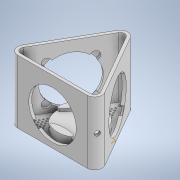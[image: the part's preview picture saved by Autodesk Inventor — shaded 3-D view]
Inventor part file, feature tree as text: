
AUTODESK INVENTOR PART (.ipt)
format: ipt  version: 2022.4 (Build 264492010, 492A)  size: 419,840 bytes
history: native  units: mm
features: sketch x11, extrude x7, pattern_circular x3, plane x2, shell x1, revolve x1, fillet x1, hole x1
ambient origin geometry x8: Origin, YZ Plane, XZ Plane, XY Plane, X Axis, Y Axis, Z Axis, Center Point
bodies: Solid1 (feature_tree)
feature tree (27):
  extrude  "Extrusion1"  Depth=37.0mm
  shell  "Shell1"  Thickness=37.0mm
  sketch  "Sketch16"  dims[d18=212.772423mm]
  extrude  "Extrusion9"  TaperAngle=30.0deg  [1 undecoded]
  sketch  "Sketch4"  dims[d12=30.0deg d13=30.0deg]
  plane  "Work Plane1"
  extrude  "Extrusion6"  TaperAngle=30.0deg  [1 undecoded]
  sketch  "Sketch11"  dims[d16=30.0deg d17=30.0deg]
  extrude  "Extrusion8"  TaperAngle=30.0deg  [1 undecoded]
  pattern_circular  "Circular Pattern3"  Angle=120.0deg  [1 undecoded]
  pattern_circular  "Circular Pattern4"  Angle=120.0deg  [1 undecoded]
  extrude  "Extrusion10"  TaperAngle=45.0deg  [1 undecoded]
  sketch  "Sketch20"  dims[d21=0.0mm]
  revolve  "Revolution4"  [1 undecoded]
  fillet  "Fillet1"  Radius=11.0mm
  plane  "Work Plane2"
  extrude  "Extrusion12"  Depth=4.0mm TaperAngle=360.0deg
  extrude  "Extrusion13"  Depth=4.0mm TaperAngle=0.0deg
  hole  "Hole3"  [1 undecoded]
  pattern_circular  "Circular Pattern7"  Count=3 Angle=360.0deg
  sketch  "Sketch1"  dims[d4=37.0mm d5=37.0mm d6=37.0mm]
  sketch  "Sketch8"  dims[d14=30.0deg d15=30.0deg]
  sketch  "Sketch19"  dims[d19=0.0mm]
  sketch  "Sketch21"  dims[d22=85.0mm d23=0.0mm]
  sketch  "Sketch24"  dims[d24=4.0mm]
  sketch  "Sketch25"  dims[d30=74.0mm]
  sketch  "Sketch26"  dims[d36=120.0deg d37=120.0deg d38=120.0deg d39=45.0deg d40=24.0mm d41=11.0mm d42=40.0mm d44=360.0deg d61=2.0mm d62=0.0mm d85=3.5mm d86=0.0mm d87=30.0mm d88=360.0deg d113=64.0mm d114=5.0mm d115=0.0mm d116=30.0mm d117=360.0deg d130=64.08588mm d131=60.0mm d132=10.0mm d133=10.0mm d140=64.856mm d141=89.0mm d142=89.0mm d143=64.856mm d144=89.0mm d145=64.856mm d146=4.0mm d147=0.0mm d148=55.5mm d149=38.75mm d150=38.75mm d151=30.0deg d153=2.0mm d193=42.5mm d194=42.5mm d195=85.0mm d196=6.5mm d197=0.0mm d198=0.0mm d199=6.25mm d200=0.0mm d201=60.0deg d202=60.0deg d203=9.0mm d204=9.0mm d205=2.0mm d206=2.0mm d207=2.0mm d208=2.0mm d209=2.0mm d210=2.0mm d211=2.0mm d212=2.0mm d213=2.0mm d214=2.0mm d215=2.0mm d216=4.0mm d217=4.0mm d218=4.0mm d219=4.0mm d220=4.0mm d221=4.0mm d222=4.0mm d223=4.0mm d224=4.0mm d225=2.0mm d227=4.0mm d228=2.0mm d229=2.0mm d230=2.0mm d231=0.0mm d232=0.0mm d233=3.7mm d234=6.0mm d235=4.0mm d236=2.0mm d237=90.0deg d238=8.0mm d239=20.594885mm d240=30.0mm d241=360.0deg]
note: 8 required parameter values undecoded (feature->parameter linkage not recoverable at this tier; creation-order binding heuristic only, values carry confidence <= 0.55)